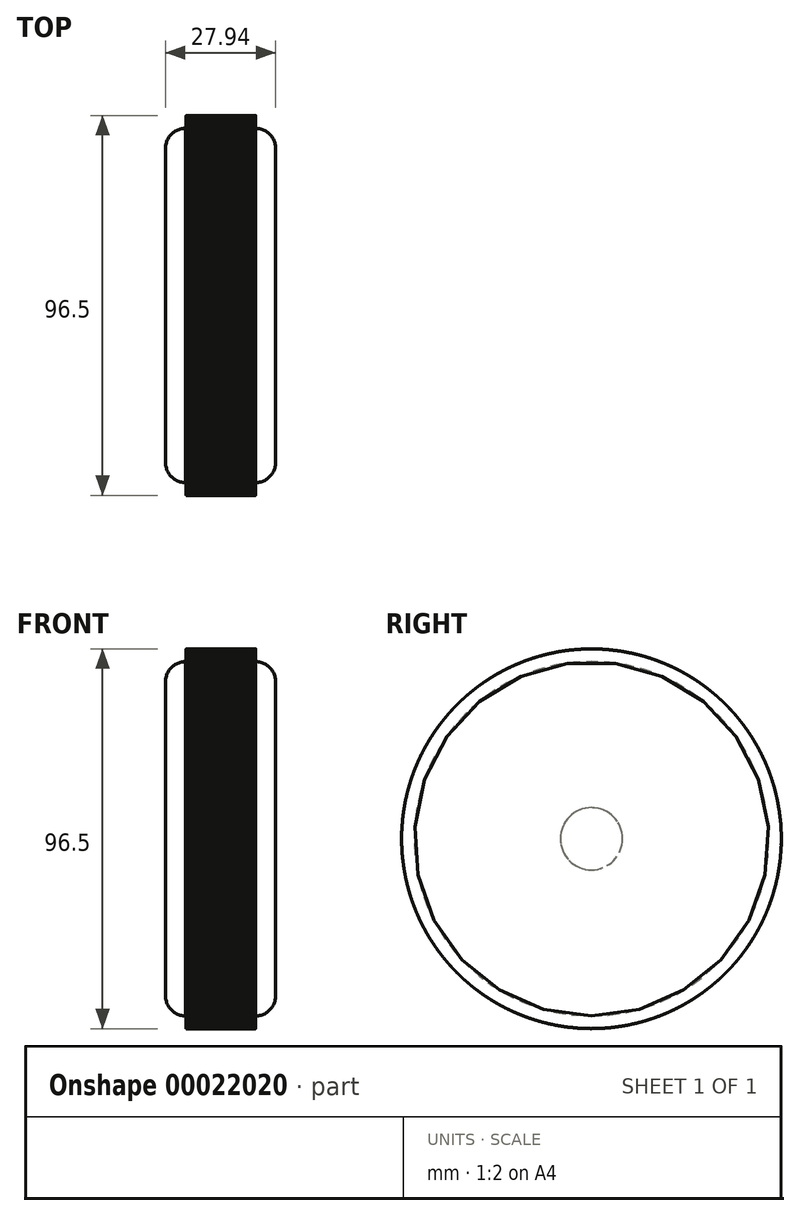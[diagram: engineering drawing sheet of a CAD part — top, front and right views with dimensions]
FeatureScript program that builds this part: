
annotation { "Feature Type Name" : "Feature", "Feature Type Description" : "" }
export const myFeature = defineFeature(function(context is Context, id is Id, definition is map)
    precondition{}
    {
        {
            var Q0;
            Q0=qCreatedBy(makeId("Right.planeOp"),FACE);
            var sketch = newSketch(context, id + "F0", { "sketchPlane" : qUnion([Q0])});
            skCircle(sketch, "E0", {"center": v(0, 0) * mm, "radius": 45 * mm});
            skSolve(sketch);
        }
        {
            var Q0;
            Q0 = qSketchRegion(id + "F0", true);
            extrude(context, id + "F1", {"entities" : qUnion([Q0]), "depth" : 5.08 * mm});
        }
        {
            var Q0;
            Q0=makeQuery(id+"F1.opExtrude","CAP_FACE",FACE,{"disambiguationData":[OSD([sQuery(id+"F0.wireOp",EDGE,"E0")])],"isStart":true});
            var sketch = newSketch(context, id + "F2", { "sketchPlane" : qUnion([Q0])});
            skCircle(sketch, "E1", {"center": v(0, 0) * mm, "radius": 7.9 * mm});
            skSolve(sketch);
        }
        {
            var Q0;
            Q0 = qSketchRegion(id + "F2", true);
            extrude(context, id + "F3", {"entities" : qUnion([Q0]), "operationType" : NewBodyOperationType.ADD, "depth" : 7.62 * mm});
        }
        {
            var Q0;
            Q0=makeQuery(id+"F3.opExtrude","CAP_FACE",FACE,{"disambiguationData":[OSD([sQuery(id+"F2.wireOp",EDGE,"E1")])],"isStart":false});
            extrude(context, id + "F4", {"entities" : qUnion([Q0]), "operationType" : NewBodyOperationType.ADD, "depth" : 10.16 * mm});
        }
        {
            var Q0;
            Q0=makeQuery(id+"F4.opExtrude","CAP_FACE",FACE,{"disambiguationData":[OSD([sQuery(id+"F2.wireOp",EDGE,"E1")])],"isStart":false});
            var sketch = newSketch(context, id + "F5", { "sketchPlane" : qUnion([Q0])});
            skCircle(sketch, "E2", {"center": v(0, 0) * mm, "radius": 45.02 * mm});
            skSolve(sketch);
        }
        {
            var Q0;
            Q0 = qSketchRegion(id + "F5", true);
            extrude(context, id + "F6", {"entities" : qUnion([Q0]), "operationType" : NewBodyOperationType.ADD, "depth" : 5.08 * mm});
        }
        {
            var Q0;
            Q0=qCreatedBy(makeId("Front.planeOp"),FACE);
            var sketch = newSketch(context, id + "F7", { "sketchPlane" : qUnion([Q0])});
            skLineSegment(sketch, "E3.bottom", {"start": v(0, 7.98) * mm, "end": v(-17.66, 7.98) * mm});
            skLineSegment(sketch, "E3.top", {"start": v(0, -7.8) * mm, "end": v(-17.66, -7.8) * mm});
            skLineSegment(sketch, "E3.left", {"start": v(0, 7.98) * mm, "end": v(0, -7.8) * mm});
            skLineSegment(sketch, "E3.right", {"start": v(-17.66, 7.98) * mm, "end": v(-17.66, -7.8) * mm});
            skSolve(sketch);
        }
        {
            var Q0;
            Q0 = qSketchRegion(id + "F7", true);
            extrude(context, id + "F8", {"entities" : qUnion([Q0]), "depth" : 48.26 * mm});
        }
        {
            var Q0;
            Q0=makeQuery(id+"F8.opExtrude","CAP_EDGE",EDGE,{"disambiguationData":[OSD([sQuery(id+"F7.wireOp",EDGE,"E3.bottom")])],"isStart":false});
            var Q1;
            Q1=makeQuery(id+"F8.opExtrude","CAP_EDGE",EDGE,{"disambiguationData":[OSD([sQuery(id+"F7.wireOp",EDGE,"E3.top")])],"isStart":false});
            fillet(context, id + "F9", {"entities" : qUnion([Q0, Q1]), "radius" : 8.38 * mm, "tangentPropagation" : true, "allowEdgeOverflow" : false});
        }
        {
            var Q0;
            Q0=makeQuery(id+"F8.opExtrude","SWEPT_BODY",BODY,{"disambiguationData":[OSD([sQuery(id+"F7.wireOp",EDGE,"E3.bottom"),sQuery(id+"F7.wireOp",EDGE,"E3.top"),sQuery(id+"F7.wireOp",EDGE,"E3.left"),sQuery(id+"F7.wireOp",EDGE,"E3.right")])]});
            var Q1;
            Q1=makeQuery(id+"F6.opExtrude","CAP_EDGE",EDGE,{"disambiguationData":[OSD([sQuery(id+"F5.wireOp",EDGE,"E2")])],"isStart":true});
            circularPattern(context, id + "F10", {"operationType" : NewBodyOperationType.ADD, "entities" : qUnion([Q0]), "axis" : qUnion([Q1]), "angle" : 23 * degree, "instanceCount" : 720});
        }
        {
            var Q0;
            Q0=makeQuery(id+"F6.opExtrude","CAP_EDGE",EDGE,{"disambiguationData":[OSD([sQuery(id+"F5.wireOp",EDGE,"E2")])],"isStart":false});
            var Q1;
            Q1=makeQuery(id+"F1.opExtrude","CAP_EDGE",EDGE,{"disambiguationData":[OSD([sQuery(id+"F0.wireOp",EDGE,"E0")])],"isStart":false});
            fillet(context, id + "F11", {"entities" : qUnion([Q0, Q1]), "radius" : 5.08 * mm, "tangentPropagation" : true, "allowEdgeOverflow" : false});
        }
    });
